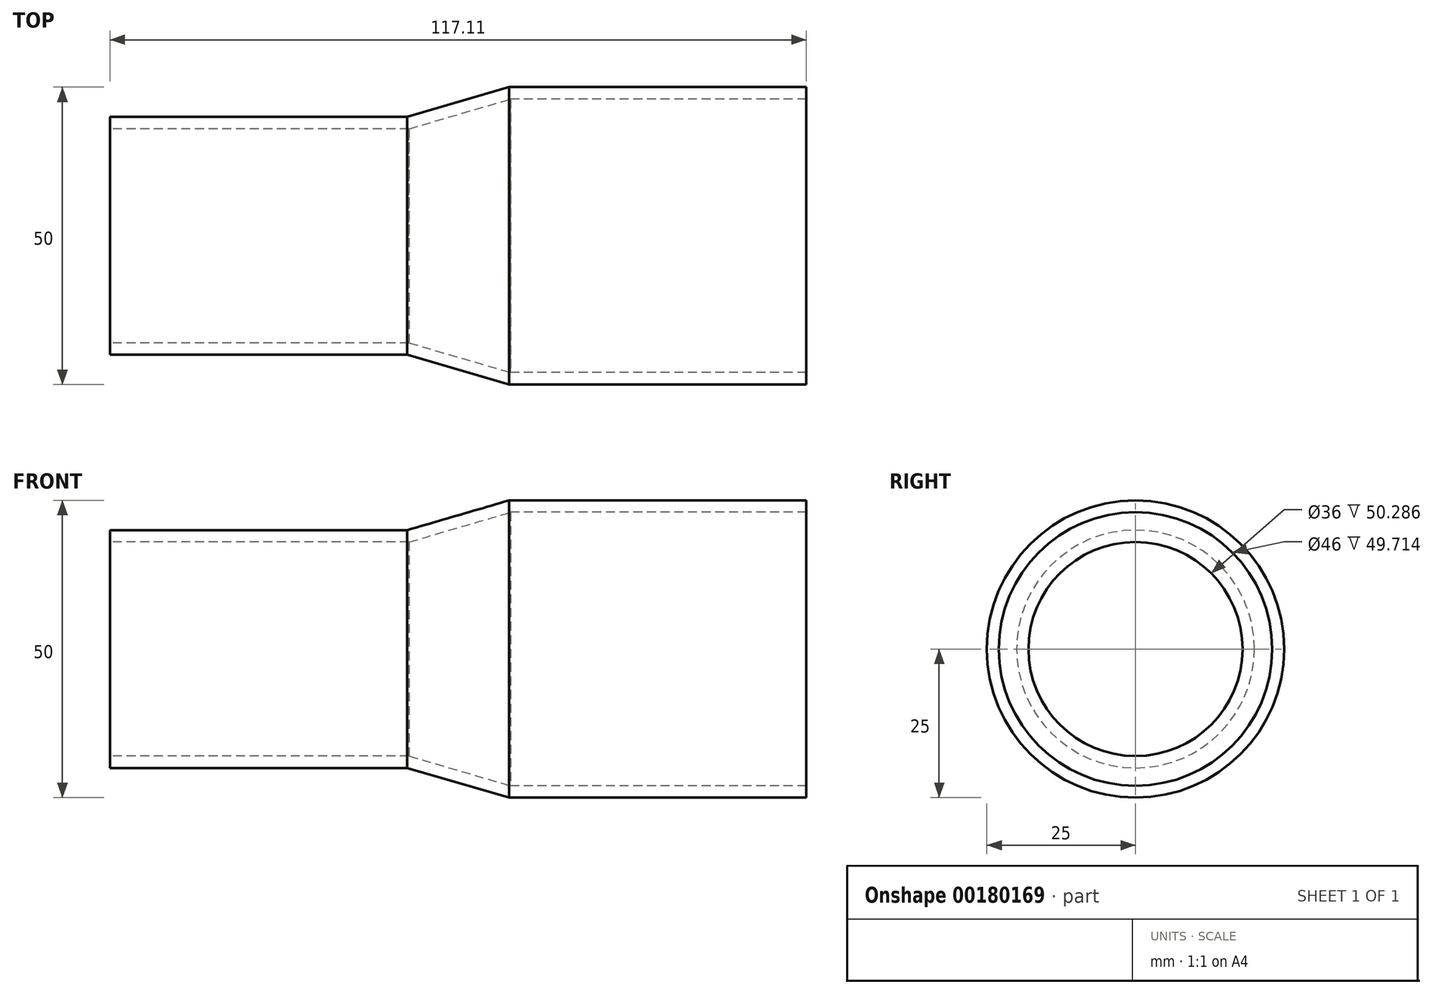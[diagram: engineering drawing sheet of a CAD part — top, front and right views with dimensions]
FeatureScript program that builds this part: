
annotation { "Feature Type Name" : "Feature", "Feature Type Description" : "" }
export const myFeature = defineFeature(function(context is Context, id is Id, definition is map)
    precondition{}
    {
        {
            var Q0;
            Q0=qCreatedBy(makeId("Front.planeOp"),FACE);
            var sketch = newSketch(context, id + "F0", { "sketchPlane" : qUnion([Q0])});
            skLineSegment(sketch, "E0", {"start": v(-49.34, 20.08) * mm, "end": v(0.66, 20.08) * mm});
            skLineSegment(sketch, "E1", {"start": v(0.66, 20.08) * mm, "end": v(17.77, 25.08) * mm});
            skLineSegment(sketch, "E2", {"start": v(17.77, 25.08) * mm, "end": v(67.77, 25.08) * mm});
            skLineSegment(sketch, "E3", {"start": v(-57.76, 0.08) * mm, "end": v(73.83, 0.08) * mm});
            skLineSegment(sketch, "E4.0", {"start": v(18.05, 23.08) * mm, "end": v(67.77, 23.08) * mm});
            skLineSegment(sketch, "E4.1", {"start": v(0.95, 18.08) * mm, "end": v(18.05, 23.08) * mm});
            skLineSegment(sketch, "E4.2", {"start": v(-49.34, 18.08) * mm, "end": v(0.95, 18.08) * mm});
            skLineSegment(sketch, "E5", {"start": v(67.77, 23.08) * mm, "end": v(67.77, 25.08) * mm});
            skLineSegment(sketch, "E6", {"start": v(-49.34, 20.08) * mm, "end": v(-49.34, 18.08) * mm});
            skSolve(sketch);
        }
        {
            var Q0;
            Q0=makeQuery(id+"F0.imprint","IMPRINT",FACE,{"disambiguationData":[TD([[makeQuery(id+"F0.imprint","IMPRINT",EDGE,{"derivedFrom":sQuery(id+"F0.wireOp",EDGE,"E0")}),-1.0]])]});
            var Q1;
            Q1=sQuery(id+"F0.wireOp",EDGE,"E3");
            revolve(context, id + "F1", {"entities" : qUnion([Q0]), "axis" : qUnion([Q1]), "revolveType" : RevolveType.FULL});
        }
    });
